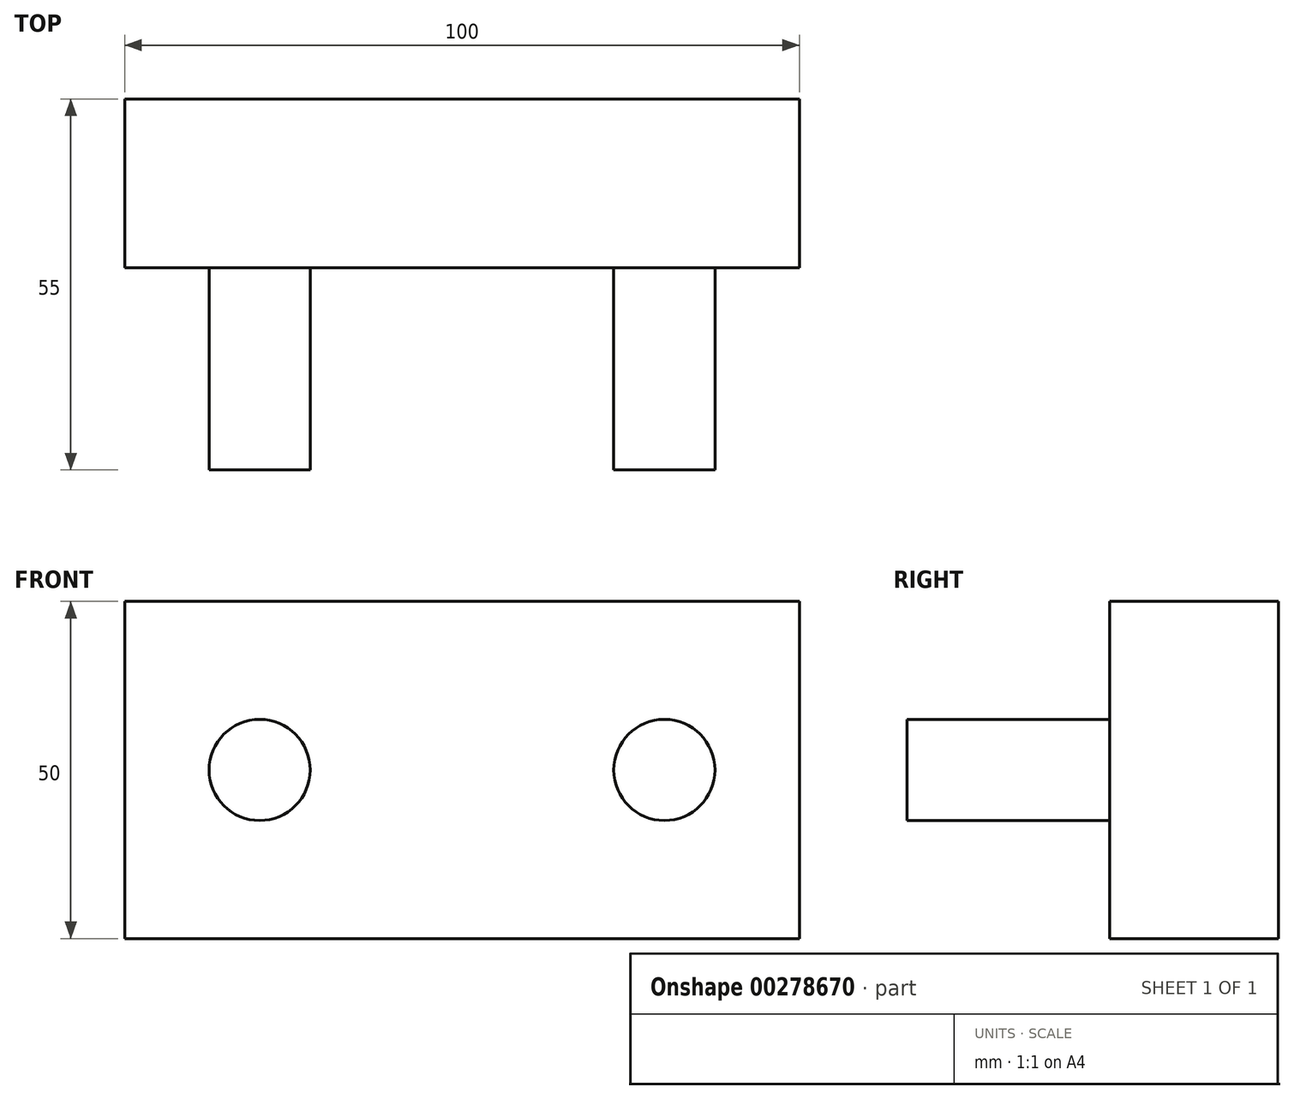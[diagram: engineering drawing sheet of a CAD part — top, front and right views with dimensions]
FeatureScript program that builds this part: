
annotation { "Feature Type Name" : "Feature", "Feature Type Description" : "" }
export const myFeature = defineFeature(function(context is Context, id is Id, definition is map)
    precondition{}
    {
        {
            var Q0;
            Q0=qCreatedBy(makeId("Front.planeOp"),FACE);
            var sketch = newSketch(context, id + "F0", { "sketchPlane" : qUnion([Q0])});
            skLineSegment(sketch, "E0.bottom", {"start": v(-50, 25) * mm, "end": v(50, 25) * mm});
            skLineSegment(sketch, "E0.top", {"start": v(-50, -25) * mm, "end": v(50, -25) * mm});
            skLineSegment(sketch, "E0.left", {"start": v(-50, 25) * mm, "end": v(-50, -25) * mm});
            skLineSegment(sketch, "E0.right", {"start": v(50, 25) * mm, "end": v(50, -25) * mm});
            skSolve(sketch);
        }
        {
            var Q0;
            Q0 = qSketchRegion(id + "F0", true);
            extrude(context, id + "F1", {"entities" : qUnion([Q0]), "depth" : 25 * mm, "offsetDistance" : 25 * mm});
        }
        {
            var Q0;
            Q0=makeQuery(id+"F1.opExtrude","CAP_FACE",FACE,{"disambiguationData":[OSD([sQuery(id+"F0.wireOp",EDGE,"E0.bottom"),sQuery(id+"F0.wireOp",EDGE,"E0.top"),sQuery(id+"F0.wireOp",EDGE,"E0.left"),sQuery(id+"F0.wireOp",EDGE,"E0.right")])],"isStart":false});
            var sketch = newSketch(context, id + "F2", { "sketchPlane" : qUnion([Q0])});
            skCircle(sketch, "E1", {"center": v(-30, 0) * mm, "radius": 7.5 * mm});
            skCircle(sketch, "E2", {"center": v(30, 0) * mm, "radius": 7.5 * mm});
            skSolve(sketch);
        }
        {
            var Q0;
            Q0 = qSketchRegion(id + "F2", true);
            extrude(context, id + "F3", {"entities" : qUnion([Q0]), "operationType" : NewBodyOperationType.ADD, "depth" : 30 * mm, "offsetDistance" : 25 * mm});
        }
    });
